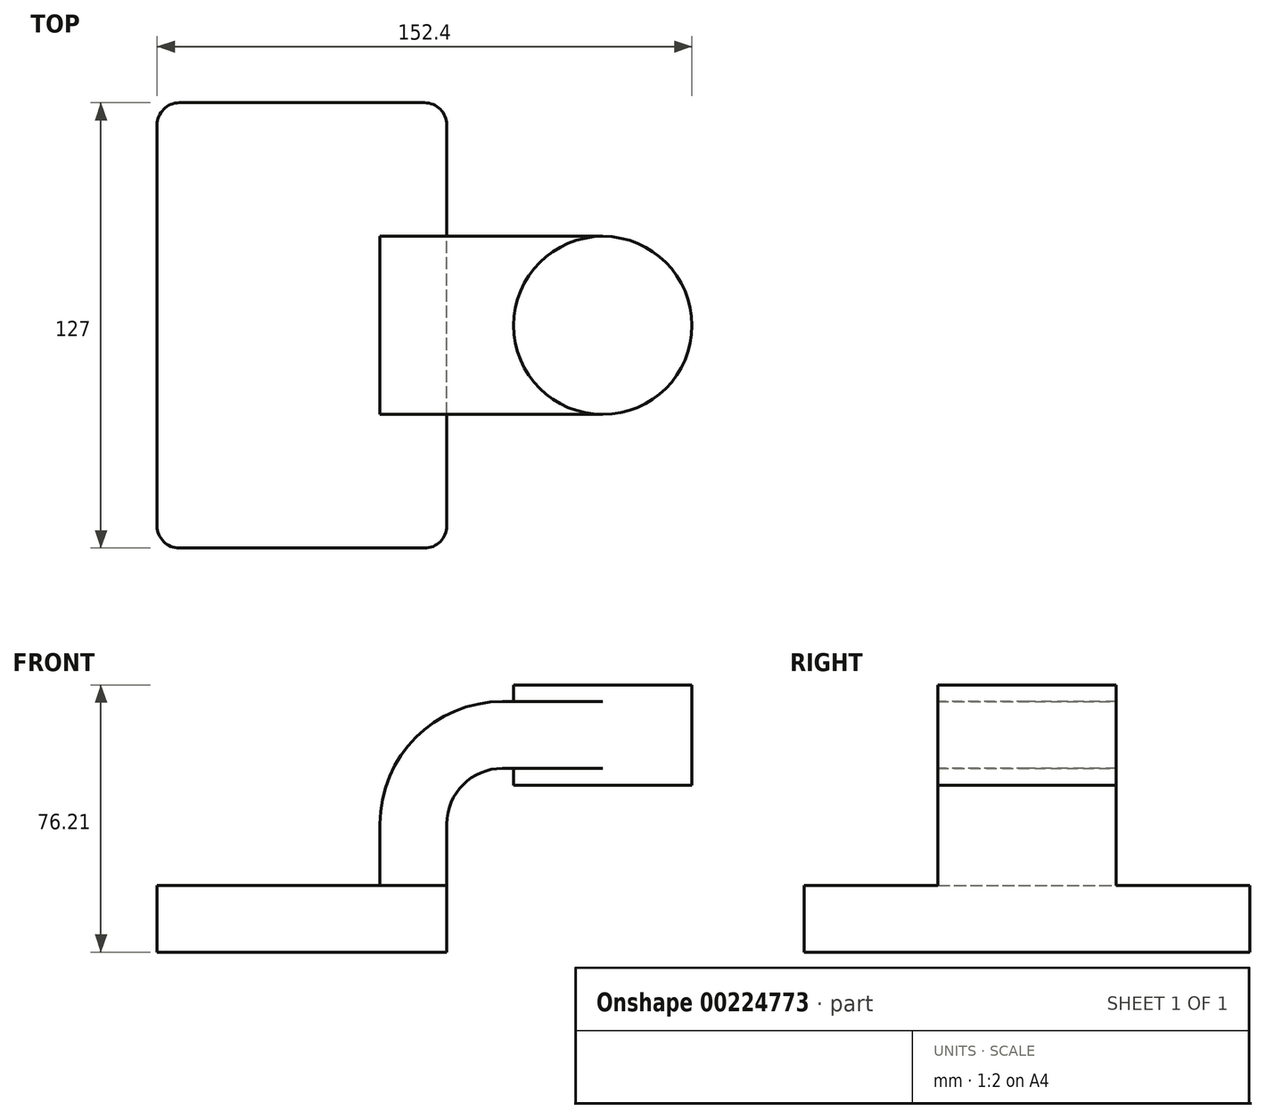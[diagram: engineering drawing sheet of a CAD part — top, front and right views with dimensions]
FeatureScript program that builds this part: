
annotation { "Feature Type Name" : "Feature", "Feature Type Description" : "" }
export const myFeature = defineFeature(function(context is Context, id is Id, definition is map)
    precondition{}
    {
        {
            var Q0;
            Q0=qCreatedBy(makeId("Front.planeOp"),FACE);
            var sketch = newSketch(context, id + "F0", { "sketchPlane" : qUnion([Q0])});
            skLineSegment(sketch, "E0.bottom", {"start": v(-41.28, 9.53) * mm, "end": v(41.28, 9.53) * mm});
            skLineSegment(sketch, "E0.top", {"start": v(-41.28, -9.53) * mm, "end": v(41.28, -9.53) * mm});
            skLineSegment(sketch, "E0.left", {"start": v(-41.28, 9.53) * mm, "end": v(-41.28, -9.53) * mm});
            skLineSegment(sketch, "E0.right", {"start": v(41.28, 9.53) * mm, "end": v(41.28, -9.53) * mm});
            skPoint(sketch, "E0.middle", {"position": v(0, 0) * mm});
            skLineSegment(sketch, "E1.bottom", {"start": v(60.33, 66.67) * mm, "end": v(111.12, 66.67) * mm});
            skLineSegment(sketch, "E1.top", {"start": v(60.32, 38.1) * mm, "end": v(111.12, 38.1) * mm});
            skLineSegment(sketch, "E1.left", {"start": v(60.33, 66.67) * mm, "end": v(60.33, 38.1) * mm});
            skLineSegment(sketch, "E1.right", {"start": v(111.12, 66.67) * mm, "end": v(111.12, 38.1) * mm});
            skPoint(sketch, "E1.middle", {"position": v(85.72, 52.39) * mm});
            skLineSegment(sketch, "E2", {"start": v(41.28, 9.53) * mm, "end": v(41.28, 27) * mm});
            skArc(sketch, "E3", {"start": v(41.28, 27) * mm, "mid": v(45.92, 38.23) * mm, "end": v(57.15, 42.88) * mm});
            skLineSegment(sketch, "E4", {"start": v(57.15, 42.88) * mm, "end": v(85.72, 42.88) * mm});
            skLineSegment(sketch, "E5.0", {"start": v(57.15, 61.93) * mm, "end": v(85.72, 61.93) * mm});
            skArc(sketch, "E5.1", {"start": v(22.23, 27) * mm, "mid": v(32.45, 51.7) * mm, "end": v(57.15, 61.93) * mm});
            skLineSegment(sketch, "E5.2", {"start": v(22.23, 9.53) * mm, "end": v(22.23, 27) * mm});
            skLineSegment(sketch, "E6", {"start": v(85.72, 38.1) * mm, "end": v(85.72, 66.67) * mm});
            skFitSpline(sketch, "E7", {"points": [v(-41.28, 9.53) * mm, v(57.15, 61.93) * mm], "startDerivative": vector(0, 91.45) * mm, "endDerivative": vector(110.46, 0) * mm});
            skSolve(sketch);
        }
        {
            var Q0;
            Q0=makeQuery(id+"F0.imprint","IMPRINT",FACE,{"disambiguationData":[TD([[makeQuery(id+"F0.imprint","IMPRINT",EDGE,{"derivedFrom":sQuery(id+"F0.wireOp",EDGE,"E0.top")}),1.0]])]});
            extrude(context, id + "F1", {"entities" : qUnion([Q0]), "depth" : 127 * mm, "symmetric" : true});
        }
        {
            var Q0;
            {var subQ1=sQuery(id+"F0.wireOp",EDGE,"E2");Q0=makeQuery(id+"F0.imprint","IMPRINT",FACE,{"disambiguationData":[TD([[makeQuery(id+"F0.imprint","IMPRINT",EDGE,{"derivedFrom":subQ1}),1.0]])]});}
            var Q1;
            {var subQ0=sQuery(id+"F0.wireOp",EDGE,"E5.0");var subQ1=sQuery(id+"F0.wireOp",EDGE,"E1.left");var subQ2=makeQuery(id+"F0.imprint","INTERSECT",VERTEX,{"derivedFrom":[subQ1,subQ0]});Q1=makeQuery(id+"F0.imprint","IMPRINT",FACE,{"disambiguationData":[TD([[makeQuery(id+"F0.imprint","IMPRINT",EDGE,{"disambiguationData":[TD([[subQ2,-1.0]])],"derivedFrom":subQ1}),1.0]])]});}
            extrude(context, id + "F2", {"entities" : qUnion([Q0, Q1]), "operationType" : NewBodyOperationType.ADD, "depth" : 50.8 * mm, "symmetric" : true});
        }
        {
            var Q0;
            Q0=makeQuery(id+"F0.imprint","IMPRINT",FACE,{"disambiguationData":[TD([[makeQuery(id+"F0.imprint","IMPRINT",EDGE,{"derivedFrom":sQuery(id+"F0.wireOp",EDGE,"E5.1")}),1.0]])]});
            extrude(context, id + "F3", {"entities" : qUnion([Q0]), "operationType" : NewBodyOperationType.ADD, "depth" : 15.88 * mm, "symmetric" : true});
        }
        {
            var Q0;
            {var subQ0=sQuery(id+"F0.wireOp",EDGE,"E1.right");Q0=makeQuery(id+"F0.imprint","IMPRINT",FACE,{"disambiguationData":[TD([[makeQuery(id+"F0.imprint","IMPRINT",EDGE,{"derivedFrom":subQ0}),-1.0]])]});}
            var Q1;
            Q1=sQuery(id+"F0.wireOp",EDGE,"E6");
            revolve(context, id + "F4", {"operationType" : NewBodyOperationType.ADD, "entities" : qUnion([Q0]), "axis" : qUnion([Q1]), "revolveType" : RevolveType.FULL});
        }
        {
            var Q0;
            Q0=makeQuery(id+"F1.opExtrude","CAP_EDGE",EDGE,{"disambiguationData":[OSD([sQuery(id+"F0.wireOp",EDGE,"E0.right")])],"isStart":false});
            var Q1;
            Q1=makeQuery(id+"F1.opExtrude","CAP_EDGE",EDGE,{"disambiguationData":[OSD([sQuery(id+"F0.wireOp",EDGE,"E0.left")])],"isStart":false});
            var Q2;
            Q2=makeQuery(id+"F1.opExtrude","CAP_EDGE",EDGE,{"disambiguationData":[OSD([sQuery(id+"F0.wireOp",EDGE,"E0.right")])],"isStart":true});
            var Q3;
            Q3=makeQuery(id+"F1.opExtrude","CAP_EDGE",EDGE,{"disambiguationData":[OSD([sQuery(id+"F0.wireOp",EDGE,"E0.left")])],"isStart":true});
            fillet(context, id + "F5", {"entities" : qUnion([Q0, Q1, Q2, Q3]), "radius" : 6.35 * mm, "tangentPropagation" : true, "allowEdgeOverflow" : false});
        }
    });
